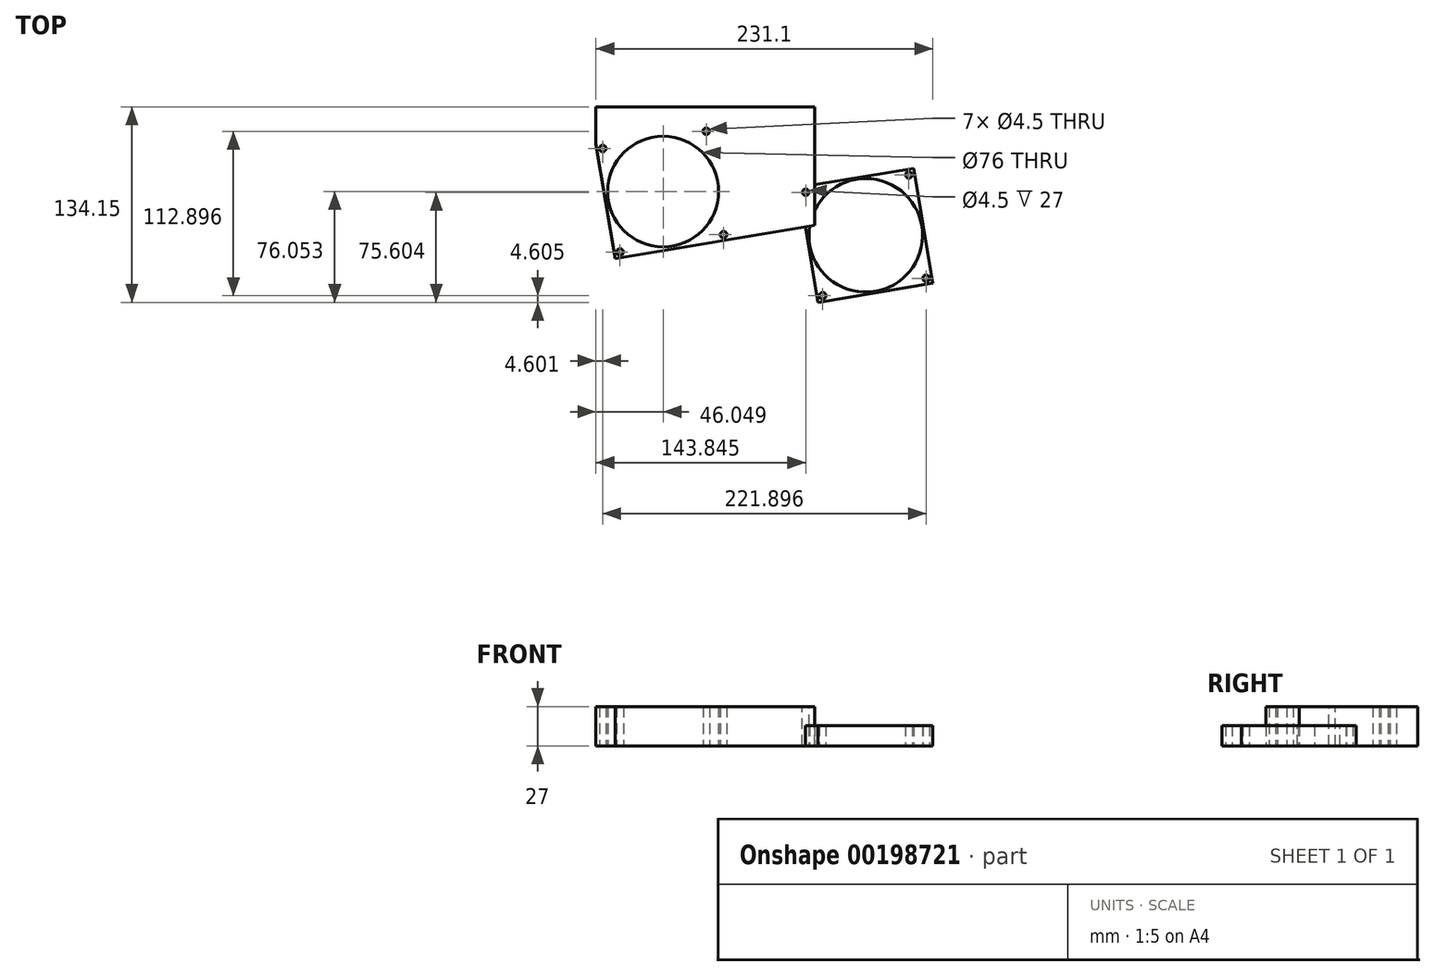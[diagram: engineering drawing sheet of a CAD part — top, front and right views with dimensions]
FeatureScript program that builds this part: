
annotation { "Feature Type Name" : "Feature", "Feature Type Description" : "" }
export const myFeature = defineFeature(function(context is Context, id is Id, definition is map)
    precondition{}
    {
        {
            var Q0;
            Q0=qCreatedBy(makeId("Top.planeOp"),FACE);
            var sketch = newSketch(context, id + "F0", { "sketchPlane" : qUnion([Q0])});
            skLineSegment(sketch, "E0.bottom", {"start": v(0, 0) * mm, "end": v(80, 0) * mm});
            skLineSegment(sketch, "E0.top", {"start": v(0, 80) * mm, "end": v(80, 80) * mm});
            skLineSegment(sketch, "E0.left", {"start": v(0, 0) * mm, "end": v(0, 80) * mm});
            skLineSegment(sketch, "E0.right", {"start": v(80, 0) * mm, "end": v(80, 80) * mm});
            skLineSegment(sketch, "E1.bottom", {"start": v(139, 50) * mm, "end": v(219, 50) * mm});
            skLineSegment(sketch, "E1.top", {"start": v(139, -30) * mm, "end": v(219, -30) * mm});
            skLineSegment(sketch, "E1.left", {"start": v(139, 50) * mm, "end": v(139, -30) * mm});
            skLineSegment(sketch, "E1.right", {"start": v(219, 50) * mm, "end": v(219, -30) * mm});
            skCircle(sketch, "E2", {"center": v(40, 40) * mm, "radius": 38 * mm});
            skCircle(sketch, "E3", {"center": v(179, 10) * mm, "radius": 39 * mm});
            skCircle(sketch, "E4", {"center": v(4, 76) * mm, "radius": 2.25 * mm});
            skCircle(sketch, "E5", {"center": v(76, 76) * mm, "radius": 2.25 * mm});
            skCircle(sketch, "E6", {"center": v(76, 4) * mm, "radius": 2.25 * mm});
            skCircle(sketch, "E7", {"center": v(4, 4) * mm, "radius": 2.25 * mm});
            skCircle(sketch, "E8", {"center": v(143, 46) * mm, "radius": 2.25 * mm});
            skCircle(sketch, "E9", {"center": v(215, 46) * mm, "radius": 2.25 * mm});
            skCircle(sketch, "E10", {"center": v(215, -26) * mm, "radius": 2.25 * mm});
            skCircle(sketch, "E11", {"center": v(143, -26) * mm, "radius": 2.25 * mm});
            skSolve(sketch);
        }
        {
            var Q0;
            Q0 = qSketchRegion(id + "F0", true);
            extrude(context, id + "F1", {"entities" : qUnion([Q0]), "depth" : 14 * mm});
        }
        {
            var Q0;
            Q0=makeQuery(id+"F1.opExtrude","SWEPT_BODY",BODY,{"disambiguationData":[OSD([sQuery(id+"F0.wireOp",EDGE,"E0.bottom"),sQuery(id+"F0.wireOp",EDGE,"E0.top"),sQuery(id+"F0.wireOp",EDGE,"E0.left"),sQuery(id+"F0.wireOp",EDGE,"E0.right"),sQuery(id+"F0.wireOp",EDGE,"E2"),sQuery(id+"F0.wireOp",EDGE,"E4"),sQuery(id+"F0.wireOp",EDGE,"E5"),sQuery(id+"F0.wireOp",EDGE,"E6"),sQuery(id+"F0.wireOp",EDGE,"E7")])]});
            var Q1;
            Q1=makeQuery(id+"F1.opExtrude","SWEPT_EDGE",EDGE,{"disambiguationData":[OSD([sQuery(id+"F0.wireOp",EDGE,"E0.bottom"),sQuery(id+"F0.wireOp",EDGE,"E0.left")])]});
            transform(context, id + "F2", {"entities" : qUnion([Q0]), "transformType" : TransformType.ROTATION, "transformAxis" : qUnion([Q1]), "angle" : 9.5 * degree, "oppositeDirection" : true, "makeCopy" : false});
        }
        {
            var Q0;
            Q0=makeQuery(id+"F1.opExtrude","SWEPT_BODY",BODY,{"disambiguationData":[OSD([sQuery(id+"F0.wireOp",EDGE,"E1.bottom"),sQuery(id+"F0.wireOp",EDGE,"E1.top"),sQuery(id+"F0.wireOp",EDGE,"E1.left"),sQuery(id+"F0.wireOp",EDGE,"E1.right"),sQuery(id+"F0.wireOp",EDGE,"E3"),sQuery(id+"F0.wireOp",EDGE,"E8"),sQuery(id+"F0.wireOp",EDGE,"E9"),sQuery(id+"F0.wireOp",EDGE,"E10"),sQuery(id+"F0.wireOp",EDGE,"E11")])]});
            var Q1;
            Q1=makeQuery(id+"F1.opExtrude","SWEPT_EDGE",EDGE,{"disambiguationData":[OSD([sQuery(id+"F0.wireOp",EDGE,"E1.top"),sQuery(id+"F0.wireOp",EDGE,"E1.left")])]});
            transform(context, id + "F3", {"entities" : qUnion([Q0]), "transformType" : TransformType.ROTATION, "transformAxis" : qUnion([Q1]), "angle" : 9.5 * degree, "oppositeDirection" : true, "makeCopy" : false});
        }
        {
            var Q0;
            Q0=makeQuery(id+"F1.opExtrude","CAP_FACE",FACE,{"disambiguationData":[OSD([sQuery(id+"F0.wireOp",EDGE,"E0.bottom"),sQuery(id+"F0.wireOp",EDGE,"E0.top"),sQuery(id+"F0.wireOp",EDGE,"E0.left"),sQuery(id+"F0.wireOp",EDGE,"E0.right"),sQuery(id+"F0.wireOp",EDGE,"E2"),sQuery(id+"F0.wireOp",EDGE,"E4"),sQuery(id+"F0.wireOp",EDGE,"E5"),sQuery(id+"F0.wireOp",EDGE,"E6"),sQuery(id+"F0.wireOp",EDGE,"E7")])],"isStart":false});
            var sketch = newSketch(context, id + "F4", { "sketchPlane" : qUnion([Q0])});
            skLineSegment(sketch, "E12", {"start": v(-13.2, 78.9) * mm, "end": v(-13.2, 104.15) * mm});
            skLineSegment(sketch, "E13", {"start": v(-13.2, 104.15) * mm, "end": v(136.8, 104.15) * mm});
            skLineSegment(sketch, "E14", {"start": v(136.8, 104.15) * mm, "end": v(136.8, 59.15) * mm});
            skLineSegment(sketch, "E15", {"start": v(78.9, 13.2) * mm, "end": v(136.93, 22.91) * mm});
            skLineSegment(sketch, "E16", {"start": v(136.93, 22.91) * mm, "end": v(136.8, 59.15) * mm});
            skSolve(sketch);
        }
        {
            var Q0;
            Q0 = qSketchRegion(id + "F4", true);
            var Q1;
            Q1=makeQuery(id+"F4.imprint","IMPRINT",FACE,{"disambiguationData":[TD([[makeQuery(id+"F4.imprint","IMPRINT",EDGE,{"derivedFrom":makeQuery(id+"F1.opExtrude","CAP_EDGE",EDGE,{"disambiguationData":[OSD([sQuery(id+"F0.wireOp",EDGE,"E0.bottom")])],"isStart":false})}),1.0]])]});
            var Q2;
            Q2=makeQuery(id+"F4.imprint","IMPRINT",FACE,{"disambiguationData":[TD([[makeQuery(id+"F4.imprint","IMPRINT",EDGE,{"derivedFrom":sQuery(id+"F4.wireOp",EDGE,"E12")}),-1.0]])]});
            extrude(context, id + "F5", {"entities" : qUnion([Q0, Q1, Q2]), "depth" : 13 * mm});
        }
        {
            var Q0;
            Q0=makeQuery(id+"F5.opExtrude","CAP_FACE",FACE,{"disambiguationData":[OSD([sQuery(id+"F0.wireOp",EDGE,"E0.bottom"),sQuery(id+"F0.wireOp",EDGE,"E0.left"),sQuery(id+"F0.wireOp",EDGE,"E2"),sQuery(id+"F0.wireOp",EDGE,"E4"),sQuery(id+"F0.wireOp",EDGE,"E5"),sQuery(id+"F0.wireOp",EDGE,"E6"),sQuery(id+"F0.wireOp",EDGE,"E7"),sQuery(id+"F4.wireOp",EDGE,"E12"),sQuery(id+"F4.wireOp",EDGE,"E13"),sQuery(id+"F4.wireOp",EDGE,"E14"),sQuery(id+"F4.wireOp",EDGE,"E15"),sQuery(id+"F4.wireOp",EDGE,"E16")])],"isStart":false});
            var sketch = newSketch(context, id + "F6", { "sketchPlane" : qUnion([Q0])});
            skCircle(sketch, "E17", {"center": v(130.65, 45.6) * mm, "radius": 2.25 * mm});
            skLineSegment(sketch, "E18", {"start": v(136.9, 32.94) * mm, "end": v(136.9, 0) * mm});
            skLineSegment(sketch, "E19", {"start": v(136.9, 0) * mm, "end": v(0, 0) * mm});
            skSolve(sketch);
        }
        {
            var Q0;
            Q0 = qSketchRegion(id + "F6", true);
            var Q1;
            {var subQ0=sQuery(id+"F6.wireOp",EDGE,"E19");Q1=makeQuery(id+"F6.imprint","IMPRINT",FACE,{"disambiguationData":[TD([[makeQuery(id+"F6.imprint","IMPRINT",EDGE,{"derivedFrom":subQ0}),-1.0]])]});}
            var Q2;
            Q2=makeQuery(id+"F1.opExtrude","CAP_FACE",FACE,{"disambiguationData":[OSD([sQuery(id+"F0.wireOp",EDGE,"E1.bottom"),sQuery(id+"F0.wireOp",EDGE,"E1.top"),sQuery(id+"F0.wireOp",EDGE,"E1.left"),sQuery(id+"F0.wireOp",EDGE,"E1.right"),sQuery(id+"F0.wireOp",EDGE,"E3"),sQuery(id+"F0.wireOp",EDGE,"E8"),sQuery(id+"F0.wireOp",EDGE,"E9"),sQuery(id+"F0.wireOp",EDGE,"E10"),sQuery(id+"F0.wireOp",EDGE,"E11")])],"isStart":false});
            extrude(context, id + "F7", {"entities" : qUnion([Q0, Q1]), "operationType" : NewBodyOperationType.REMOVE, "endBound" : BoundingType.UP_TO_SURFACE, "oppositeDirection" : true, "endBoundEntityFace" : qUnion([Q2]), "depth" : 25 * mm});
        }
        {
            var Q0;
            Q0=makeQuery(id+"F5.opExtrude","CAP_FACE",FACE,{"disambiguationData":[OSD([sQuery(id+"F0.wireOp",EDGE,"E0.bottom"),sQuery(id+"F0.wireOp",EDGE,"E0.left"),sQuery(id+"F0.wireOp",EDGE,"E2"),sQuery(id+"F0.wireOp",EDGE,"E4"),sQuery(id+"F0.wireOp",EDGE,"E5"),sQuery(id+"F0.wireOp",EDGE,"E6"),sQuery(id+"F0.wireOp",EDGE,"E7"),sQuery(id+"F4.wireOp",EDGE,"E12"),sQuery(id+"F4.wireOp",EDGE,"E13"),sQuery(id+"F4.wireOp",EDGE,"E14"),sQuery(id+"F4.wireOp",EDGE,"E15"),sQuery(id+"F4.wireOp",EDGE,"E16")])],"isStart":true});
            extrude(context, id + "F8", {"entities" : qUnion([Q0]), "operationType" : NewBodyOperationType.ADD, "depth" : 14 * mm});
        }
    });
